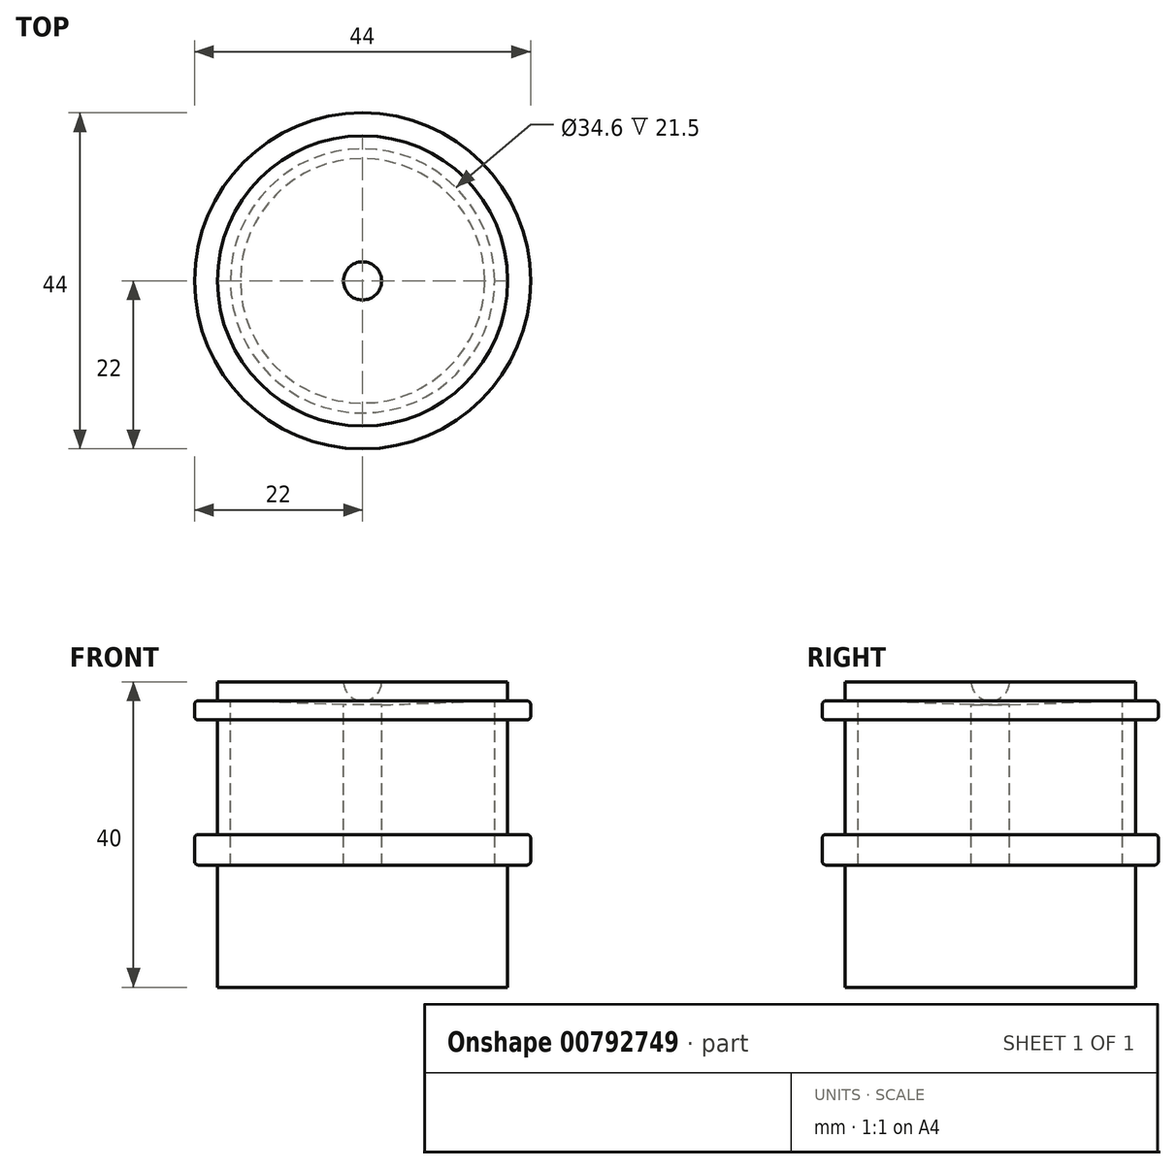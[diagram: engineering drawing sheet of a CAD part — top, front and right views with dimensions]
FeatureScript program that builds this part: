
annotation { "Feature Type Name" : "Feature", "Feature Type Description" : "" }
export const myFeature = defineFeature(function(context is Context, id is Id, definition is map)
    precondition{}
    {
        {
            var Q0;
            Q0=qCreatedBy(makeId("Front.planeOp"),FACE);
            var sketch = newSketch(context, id + "F0", { "sketchPlane" : qUnion([Q0])});
            skLineSegment(sketch, "E0", {"start": v(0, 20.24) * mm, "end": v(0, -27.02) * mm, "construction": true});
            skLineSegment(sketch, "E1.bottom", {"start": v(16, 16.13) * mm, "end": v(19, 16.13) * mm});
            skLineSegment(sketch, "E1.top", {"start": v(0, -23.87) * mm, "end": v(19, -23.87) * mm});
            skLineSegment(sketch, "E1.left", {"start": v(0, 16.13) * mm, "end": v(0, -23.87) * mm});
            skLineSegment(sketch, "E1.right", {"start": v(19, 16.13) * mm, "end": v(19, -23.87) * mm});
            skLineSegment(sketch, "E2.bottom", {"start": v(16, 13.63) * mm, "end": v(21.5, 13.63) * mm});
            skLineSegment(sketch, "E2.top", {"start": v(16, 11.13) * mm, "end": v(21.5, 11.13) * mm});
            skLineSegment(sketch, "E2.left", {"start": v(0, 13.63) * mm, "end": v(0, 11.13) * mm});
            skLineSegment(sketch, "E2.right", {"start": v(22, 13.13) * mm, "end": v(22, 11.63) * mm});
            skLineSegment(sketch, "E3.bottom", {"start": v(16, -3.87) * mm, "end": v(21.5, -3.87) * mm});
            skLineSegment(sketch, "E3.top", {"start": v(16, -7.87) * mm, "end": v(21.5, -7.87) * mm});
            skLineSegment(sketch, "E3.left", {"start": v(0, -3.87) * mm, "end": v(0, -7.87) * mm});
            skLineSegment(sketch, "E3.right", {"start": v(22, -4.37) * mm, "end": v(22, -7.37) * mm});
            skLineSegment(sketch, "E4.bottom", {"start": v(16, 16.13) * mm, "end": v(17.3, 16.13) * mm});
            skLineSegment(sketch, "E4.top", {"start": v(0, -23.87) * mm, "end": v(17.3, -23.87) * mm});
            skLineSegment(sketch, "E4.right", {"start": v(17.3, 16.13) * mm, "end": v(17.3, -23.87) * mm});
            skLineSegment(sketch, "E5.top", {"start": v(0, -23.87) * mm, "end": v(16, -23.87) * mm});
            skLineSegment(sketch, "E5.right", {"start": v(16, 16.13) * mm, "end": v(16, -23.87) * mm});
            skArc(sketch, "E6", {"start": v(0, 13.63) * mm, "mid": v(1.77, 14.37) * mm, "end": v(2.5, 16.13) * mm});
            skLineSegment(sketch, "E7.bottom", {"start": v(0, 10.67) * mm, "end": v(2.5, 10.67) * mm});
            skLineSegment(sketch, "E7.top", {"start": v(0, 0) * mm, "end": v(2.5, 0) * mm});
            skLineSegment(sketch, "E7.left", {"start": v(0, 10.67) * mm, "end": v(0, 0) * mm});
            skLineSegment(sketch, "E7.right", {"start": v(17.3, 10.67) * mm, "end": v(17.3, 0) * mm});
            skArc(sketch, "E8", {"start": v(17.3, 6.63) * mm, "mid": v(16, 5.33) * mm, "end": v(17.3, 4.03) * mm});
            skLineSegment(sketch, "E9", {"start": v(2.5, 16.13) * mm, "end": v(2.5, -23.87) * mm});
            skLineSegment(sketch, "E10.trimOffspring", {"start": v(16, 10.67) * mm, "end": v(17.3, 10.67) * mm});
            skLineSegment(sketch, "E11.trimOffspring", {"start": v(16, 0) * mm, "end": v(17.3, 0) * mm});
            skLineSegment(sketch, "E12", {"start": v(16, 16.13) * mm, "end": v(2.5, 16.13) * mm});
            skPoint(sketch, "E13.visualSharp", {"position": v(22, -3.87) * mm});
            skArc(sketch, "E13.filletArc", {"start": v(22, -4.37) * mm, "mid": v(21.85, -4.01) * mm, "end": v(21.5, -3.87) * mm});
            skPoint(sketch, "E14.visualSharp", {"position": v(22, -7.87) * mm});
            skArc(sketch, "E14.filletArc", {"start": v(21.5, -7.87) * mm, "mid": v(21.85, -7.72) * mm, "end": v(22, -7.37) * mm});
            skPoint(sketch, "E15.visualSharp", {"position": v(22, 13.63) * mm});
            skArc(sketch, "E15.filletArc", {"start": v(22, 13.13) * mm, "mid": v(21.85, 13.49) * mm, "end": v(21.5, 13.63) * mm});
            skPoint(sketch, "E16.visualSharp", {"position": v(22, 11.13) * mm});
            skArc(sketch, "E16.filletArc", {"start": v(21.5, 11.13) * mm, "mid": v(21.85, 11.28) * mm, "end": v(22, 11.63) * mm});
            skLineSegment(sketch, "E17", {"start": v(16, -7.87) * mm, "end": v(0, -7.87) * mm});
            skLineSegment(sketch, "E18", {"start": v(16, -3.87) * mm, "end": v(0, -3.87) * mm});
            skLineSegment(sketch, "E19", {"start": v(16, 11.13) * mm, "end": v(2.5, 10.67) * mm});
            skLineSegment(sketch, "E20", {"start": v(16, 13.63) * mm, "end": v(2.5, 13.1) * mm});
            skSolve(sketch);
        }
        {
            var Q0;
            Q0 = qSketchRegion(id + "F0", true);
            var Q1;
            Q1=sQuery(id+"F0.wireOp",EDGE,"E0");
            revolve(context, id + "F1", {"surfaceOperationType" : NewSurfaceOperationType.NEW, "entities" : qUnion([Q0]), "axis" : qUnion([Q1]), "revolveType" : RevolveType.FULL});
        }
    });
